# Revit family: Haworth_Compose_Worksurface_RectangularConvergent
name_source: partatom
category: Furniture Systems
revit_build: Autodesk Revit 2018 (Build: 20170223_1515(x64)
units: mm (PartAtom-declared; Revit-internal decimal feet)

## family parameters
Always vertical = Yes
Cut with Voids When Loaded = No
OmniClass Number = 23.40.70.14.64.21.21
OmniClass Title = Desk System
Part Type = Normal
Room Calculation Point = No
Round Connector Dimension = Use Diameter
Shared = No
Work Plane-Based = No

## types (21) — shared parameters
Actual Height = 29"
Assembly Code = E2020200
Cantilever Support Location = 1 3/4"
Custom Size = No
Deep Worksurface Thickness = No
Description = Haworth - Worksurface - Compose Convergent - Rectangular
Disc Base Support = No
Double Support Leg = Yes
End = Yes
End Support Location = 1 3/4"
Height = 29"
Leg Location = 15"
Manufacturer = Haworth
Max. Depth = 36"
Max. Height = 42"
Max. Width = 72"
Min. Depth = 24"
Min. Height = 26"
Min. Width = 36"
Model = WURV
Revision Number = 6
Size = Verify Final Dim. w/ Haworth
Standard Length = 36-72 in. @ 6 in. increments
Standard Widths = 24, 30, 36 in.
Standard Worksurface Thickness = Yes
Support Column = No
Support Finish = Haworth _ Paint _ Metallic Champagne
Support Height = 27 13/16"
Support P Leg = No
Support Panel = No
Support Post_45 Degree = No
Support Post_90 Degree = No
Sustainability Info = http://media.haworth.com
Top Thickness = 1 3/16"
URL = www.haworth.com
URL - Product = http://www.haworth.com
Warranty = http://www.haworth.com
Worksurface Edge Finish = Haworth _ Laminate _ Maple H-AE
Worksurface Finish = Haworth _ Laminate _ Maple H-AE

## per-type parameters (varying)
| type | Actual Length | Actual Width | Length | Width |
| 36L 24w | 36" | 24" | 36" | 24" |
| 42L 24w | 42" | 24" | 42" | 24" |
| 48L 24w | 48" | 24" | 48" | 24" |
| 54L 24w | 54" | 24" | 54" | 24" |
| 60L 24w | 60" | 24" | 60" | 24" |
| 66L 24w | 66" | 24" | 66" | 24" |
| 72L 24w | 72" | 24" | 72" | 24" |
| 36L 30w | 36" | 30" | 36" | 30" |
| 42L 30w | 42" | 30" | 42" | 30" |
| 48L 30w | 48" | 30" | 48" | 30" |
| 54L 30w | 54" | 30" | 54" | 30" |
| 60L 30w | 60" | 30" | 60" | 30" |
| 66L 30w | 66" | 30" | 66" | 30" |
| 72L 30w | 72" | 30" | 72" | 30" |
| 36L 36w | 36" | 36" | 36" | 36" |
| 42L 36w | 42" | 36" | 42" | 36" |
| 48L 36w | 48" | 36" | 48" | 36" |
| 54L 36w | 54" | 36" | 54" | 36" |
| 60L 36w | 60" | 36" | 60" | 36" |
| 66L 36w | 66" | 36" | 66" | 36" |
| 72L 36w | 72" | 36" | 72" | 36" |

## geometry (parser evidence)
native form markers: Sweep x16
no freeform markers — native parametric forms only
